# Revit family: IS_Contour21_S2406_BIM_DE
name_source: partatom
category: Plumbing Fixtures
revit_build: Autodesk Revit MEP 2016 (Build: 20161004_0715(x64)
units: mm (PartAtom-declared; Revit-internal decimal feet)

## family parameters
Always vertical = No
Cut with Voids When Loaded = No
OmniClass Number = 23.45.05.14.14
OmniClass Title = Sinks/Lavatories
Part Type = Normal
Room Calculation Point = No
Round Connector Dimension = Use Diameter
Shared = No
Work Plane-Based = No

## types (2) — shared parameters
Accessories = www.idealstandard.de\ersatzteile
AssetType = Fixed
BIMobject category = Basins
BOSUseNativeGeometries = 1
Brand = Ideal Standard
Brand url = http://www.idealstandard.de
CodePerformance = DIN EN 14688 CL 00, DIN EN 31, DIN
ConnectionType = Plumbing
CurrencyUnit = €
CurrentRevision = 1
Date of publishing = 20/12/2017
DurationUnit = Year
Edition number = 1
ExpectedLife = 25
IFC Classification = Sanitary Terminal
IfcExportAs = IfcSanitaryTerminalType
Installation instructions = http://www.idealstandard.de
InstallationInstructions = www.idealstandard.de\produkte
MaintenanceInformation = www.idealstandard.de\produkte
Manufacturer name = Ideal Standard
ManufacturerURL = http://www.idealstandard.de
Material = Vitreous china
Material main = Ceramics
NBS Reference Code = 35-79-93
NBS Reference Description = Wall-Hung Hand Rinse Basins
NettWeight = 9.61 Kg
Nominal height = 177
Nominal width = 400
NominalDepth = 365 mm
NominalHeight = 177 mm
NominalLength = 365 mm
NominalWidth = 399 mm
OmniClass Code = 23-31 13 00
OmniClass Description = Sinks
Product Guid = 865e24fd-99c1-45d3-b77e-8d7fa6e9820e
Product SKU = S2406
Product data url = https://bimobject.com
Product family = Sanitary
Product group = Basin
Product name = CONTOUR21 handrinse washbasin 400x365mm, 1 taphole, no overflow
Product url = http://www.idealstandard.de
ProductInformation = www.idealstandard.de/produkte
QR code = http://bimobject.com
Shape = Sculptured
Size = 177 x 365 x 400mm
Space = Internal
SpareParts = www.idealstandard.de/ersatzteile
Technical description = http://www.idealstandard.de
URL = http://www.idealstandard.de
Uniclass 1.4 Code = L7212
Uniclass 1.4 Description = Washbasins
Uniclass 2.0 Code = PR-35-79-93
Uniclass 2.0 Description = Wall-Hung Hand Rinse Basins
Uniclass 2015 Code = Pr_40_20_96_95
Uniclass 2015 Name = Wall-hung hand rinse basins
Uniclass2015Code = Pr_40_20_96_95
Uniclass2015Title = Wall-hung hand rinse basins
Uniclass2015Version = Products v1.1
Version = 1
VolumeUnits = Litres
Weight Net (Kg) = 9.61
zero-valued in all types: Cost, DrainSize

## per-type parameters (varying)
| type | BIMObjectName | BarCode | Color | Description | EAN code | Features | Finish | MainColor | Model | ModelNumber | ModelReference | Name |
| S240601 - CONTOUR21 handrinse washbasin 400x365mm, 1 taphole, no overflow | ISI_IdealStandard_Wall-HungHandRinseBasins_Contour21_S240601 | 5017830398806 | White | IS Handwaschbecken CONTOUR 21, 1 Hl., o.Ül., 400x365x177mm, Weiß | https://5017830398806 | IS Handwaschbecken CONTOUR 21, 1 Hl., o.Ül., 400x365x177mm, Weiß | White | White | S240601 | S240601 | IS Handwaschbecken CONTOUR 21, 1 Hl., o.Ül., 400x365x177mm, Weiß | Wall-HungHandRinseBasins_Contour21_S240601 |
| S2406MA - CONTOUR21 handrinse washbasin 400x365mm, 1 taphole, no overflow | ISI_IdealStandard_Wall-HungHandRinseBasins_Contour21_S2406MA | 5017830506676 | WHITE IP | IS Handwaschbecken CONTOUR 21, 1 Hl., o.Ül., 400x365x177mm, Weiß m.Ideal Plus | https://5017830506676 | IS Handwaschbecken CONTOUR 21, 1 Hl., o.Ül., 400x365x177mm, Weiß m.Ideal Plus | WHITE IP | WHITE IP | S2406MA | S2406MA | IS Handwaschbecken CONTOUR 21, 1 Hl., o.Ül., 400x365x177mm, Weiß m.Ideal Plus | Wall-HungHandRinseBasins_Contour21_S2406MA |

## geometry (parser evidence)
native form markers: Blend x4, Sweep x2
no freeform markers — native parametric forms only
